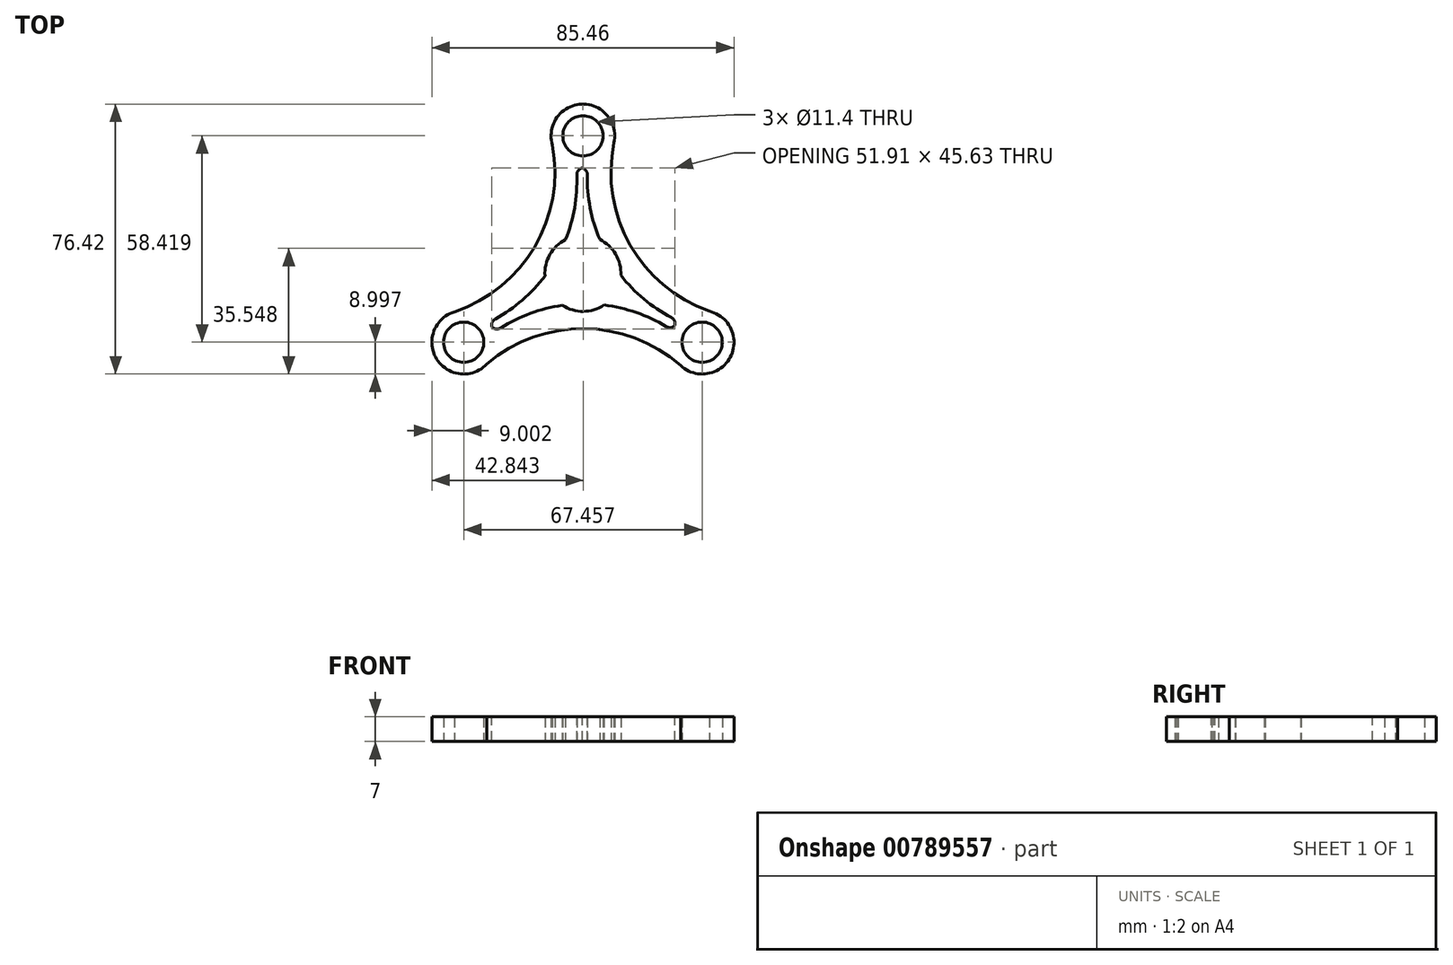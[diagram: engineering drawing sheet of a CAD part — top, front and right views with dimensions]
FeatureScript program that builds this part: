
annotation { "Feature Type Name" : "Feature", "Feature Type Description" : "" }
export const myFeature = defineFeature(function(context is Context, id is Id, definition is map)
    precondition{}
    {
        {
            var Q0;
            Q0=qCreatedBy(makeId("Top.planeOp"),FACE);
            var sketch = newSketch(context, id + "F0", { "sketchPlane" : qUnion([Q0])});
            skCircle(sketch, "E0", {"center": v(0, 0) * mm, "radius": 10.75 * mm});
            skCircle(sketch, "E1", {"center": v(0, 38.95) * mm, "radius": 5.7 * mm});
            skArc(sketch, "E2", {"start": v(8.77, 36.94) * mm, "mid": v(-0.3, 47.94) * mm, "end": v(-8.62, 36.35) * mm});
            skCircle(sketch, "E3.1.0", {"center": v(-33.73, -19.47) * mm, "radius": 5.7 * mm});
            skArc(sketch, "E3.1.1", {"start": v(-25.17, -16.7) * mm, "mid": v(-25.8, -15.2) * mm, "end": v(-26.7, -13.86) * mm});
            skCircle(sketch, "E3.2.0", {"center": v(33.73, -19.47) * mm, "radius": 5.7 * mm});
            skArc(sketch, "E3.2.1", {"start": v(27.6, -26.07) * mm, "mid": v(41.67, -23.7) * mm, "end": v(35.79, -10.71) * mm});
            skLineSegment(sketch, "E4", {"start": v(0, 38.95) * mm, "end": v(17.64, -3.14) * mm, "construction": true});
            skLineSegment(sketch, "E5", {"start": v(33.73, -19.47) * mm, "end": v(8.7, 13.34) * mm, "construction": true});
            skLineSegment(sketch, "E6", {"start": v(13.22, 7.4) * mm, "end": v(7.73, 49.98) * mm, "construction": true});
            skLineSegment(sketch, "E7", {"start": v(13.22, 7.4) * mm, "end": v(44.06, -16.02) * mm, "construction": true});
            skArc(sketch, "E8", {"start": v(8.77, 36.94) * mm, "mid": v(13.37, 8.06) * mm, "end": v(35.79, -10.71) * mm});
            skArc(sketch, "E9.1.0", {"start": v(-36.37, -10.87) * mm, "mid": v(-13.66, 7.55) * mm, "end": v(-8.62, 36.35) * mm});
            skArc(sketch, "E9.2.0", {"start": v(27.6, -26.07) * mm, "mid": v(0.3, -15.6) * mm, "end": v(-27.17, -25.64) * mm});
            skLineSegment(sketch, "E10", {"start": v(0, 0) * mm, "end": v(33.73, -19.47) * mm, "construction": true});
            skLineSegment(sketch, "E11", {"start": v(0, 0) * mm, "end": v(-33.73, -19.47) * mm, "construction": true});
            skArc(sketch, "E12", {"start": v(1.34, 30.05) * mm, "mid": v(1.84, 19.65) * mm, "end": v(4.75, 9.65) * mm});
            skArc(sketch, "E13.1.0", {"start": v(-26.7, -13.86) * mm, "mid": v(-17.94, -8.23) * mm, "end": v(-10.73, -0.71) * mm});
            skArc(sketch, "E13.2.0", {"start": v(25.35, -16.18) * mm, "mid": v(16.1, -11.42) * mm, "end": v(5.98, -8.93) * mm});
            skArc(sketch, "E14.trimOffspring", {"start": v(10.74, -0.53) * mm, "mid": v(18.12, -7.95) * mm, "end": v(27.04, -13.45) * mm});
            skArc(sketch, "E15.trimOffspring", {"start": v(-4.91, 9.56) * mm, "mid": v(-2.18, 19.67) * mm, "end": v(-1.87, 30.14) * mm});
            skArc(sketch, "E16.trimOffspring", {"start": v(-5.82, -9.04) * mm, "mid": v(-15.95, -11.72) * mm, "end": v(-25.17, -16.7) * mm});
            skArc(sketch, "E17.trimOffspring", {"start": v(-36.37, -10.87) * mm, "mid": v(-41.37, -24.23) * mm, "end": v(-27.17, -25.64) * mm});
            skPoint(sketch, "E18.orphan", {"position": v(34.45, -13.82) * mm});
            skArc(sketch, "E19.trimOffspring", {"start": v(27.04, -13.45) * mm, "mid": v(26.07, -14.74) * mm, "end": v(25.35, -16.18) * mm});
            skPoint(sketch, "E20.orphan", {"position": v(5.36, 37) * mm});
            skArc(sketch, "E21.trimOffspring", {"start": v(-1.87, 30.14) * mm, "mid": v(-0.27, 29.95) * mm, "end": v(1.34, 30.05) * mm});
            skSolve(sketch);
        }
        {
            var Q0;
            Q0=makeQuery(id+"F0.imprint","IMPRINT",FACE,{"disambiguationData":[TD([[makeQuery(id+"F0.imprint","IMPRINT",EDGE,{"derivedFrom":sQuery(id+"F0.wireOp",EDGE,"E1")}),-1.0]])]});
            extrude(context, id + "F1", {"entities" : qUnion([Q0]), "depth" : 7 * mm, "offsetDistance" : 25 * mm});
        }
        {
            var Q0;
            Q0=makeQuery(id+"F1.opExtrude","SWEPT_EDGE",EDGE,{"disambiguationData":[OSD([sQuery(id+"F0.wireOp",EDGE,"E12"),sQuery(id+"F0.wireOp",EDGE,"E21.trimOffspring")])]});
            var Q1;
            Q1=makeQuery(id+"F1.opExtrude","SWEPT_EDGE",EDGE,{"disambiguationData":[OSD([sQuery(id+"F0.wireOp",EDGE,"E15.trimOffspring"),sQuery(id+"F0.wireOp",EDGE,"E21.trimOffspring")])]});
            var Q2;
            Q2=makeQuery(id+"F1.opExtrude","SWEPT_EDGE",EDGE,{"disambiguationData":[OSD([sQuery(id+"F0.wireOp",EDGE,"E13.2.0"),sQuery(id+"F0.wireOp",EDGE,"E19.trimOffspring")])]});
            var Q3;
            Q3=makeQuery(id+"F1.opExtrude","SWEPT_EDGE",EDGE,{"disambiguationData":[OSD([sQuery(id+"F0.wireOp",EDGE,"E14.trimOffspring"),sQuery(id+"F0.wireOp",EDGE,"E19.trimOffspring")])]});
            var Q4;
            Q4=makeQuery(id+"F1.opExtrude","SWEPT_EDGE",EDGE,{"disambiguationData":[OSD([sQuery(id+"F0.wireOp",EDGE,"E3.1.1"),sQuery(id+"F0.wireOp",EDGE,"E13.1.0")])]});
            var Q5;
            Q5=makeQuery(id+"F1.opExtrude","SWEPT_EDGE",EDGE,{"disambiguationData":[OSD([sQuery(id+"F0.wireOp",EDGE,"E3.1.1"),sQuery(id+"F0.wireOp",EDGE,"E16.trimOffspring")])]});
            fillet(context, id + "F2", {"entities" : qUnion([Q0, Q1, Q2, Q3, Q4, Q5]), "radius" : 2 * mm, "tangentPropagation" : true, "allowEdgeOverflow" : false});
        }
    });
